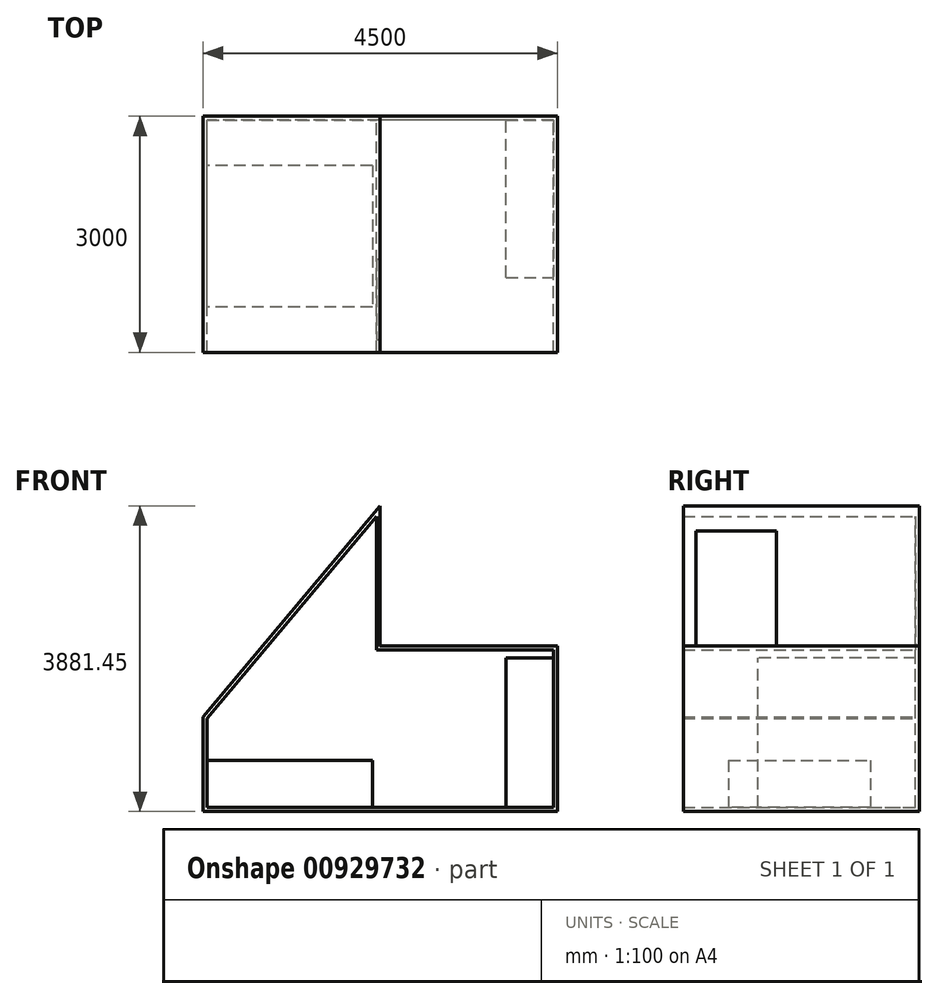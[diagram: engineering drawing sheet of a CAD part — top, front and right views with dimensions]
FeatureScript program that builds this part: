
annotation { "Feature Type Name" : "Feature", "Feature Type Description" : "" }
export const myFeature = defineFeature(function(context is Context, id is Id, definition is map)
    precondition{}
    {
        {
            var Q0;
            Q0=qCreatedBy(makeId("Front.planeOp"),FACE);
            var sketch = newSketch(context, id + "F0", { "sketchPlane" : qUnion([Q0])});
            skLineSegment(sketch, "E0.bottom", {"start": v(98.96, 0) * mm, "end": v(-4401.04, 0) * mm});
            skLineSegment(sketch, "E0.top", {"start": v(98.96, 2100) * mm, "end": v(-2151.04, 2100) * mm});
            skLineSegment(sketch, "E0.left", {"start": v(98.96, 0) * mm, "end": v(98.96, 2100) * mm});
            skLineSegment(sketch, "E0.right", {"start": v(-4401.04, 0) * mm, "end": v(-4401.04, 1200) * mm});
            skLineSegment(sketch, "E1", {"start": v(-4401.04, 1200) * mm, "end": v(-2151.04, 3881.45) * mm});
            skPoint(sketch, "E1.endSnap0", {"position": v(-2151.04, 2100) * mm});
            skLineSegment(sketch, "E2", {"start": v(-2151.04, 3881.45) * mm, "end": v(-2151.04, 2100) * mm});
            skPoint(sketch, "E3.orphan", {"position": v(-4401.04, 2100) * mm});
            skSolve(sketch);
        }
        {
            var Q0;
            Q0 = qSketchRegion(id + "F0", true);
            extrude(context, id + "F1", {"entities" : qUnion([Q0]), "depth" : 3000 * mm, "offsetDistance" : 25 * mm});
        }
        {
            var Q0;
            Q0=makeQuery(id+"F1.opExtrude","CAP_FACE",FACE,{"disambiguationData":[OSD([sQuery(id+"F0.wireOp",EDGE,"E0.bottom"),sQuery(id+"F0.wireOp",EDGE,"E0.top"),sQuery(id+"F0.wireOp",EDGE,"E0.left"),sQuery(id+"F0.wireOp",EDGE,"E0.right"),sQuery(id+"F0.wireOp",EDGE,"E1"),sQuery(id+"F0.wireOp",EDGE,"E2")])],"isStart":false});
            shell(context, id + "F2", {"entities" : qUnion([Q0]), "thickness" : 50 * mm});
        }
        {
            var Q0;
            Q0=makeQuery(id+"F1.opExtrude","SWEPT_FACE",FACE,{"disambiguationData":[OSD([sQuery(id+"F0.wireOp",EDGE,"E2")])]});
            var sketch = newSketch(context, id + "F3", { "sketchPlane" : qUnion([Q0])});
            skPoint(sketch, "E4.middle", {"position": v(-1500, 2100) * mm});
            skPoint(sketch, "E4.top.start.orphan", {"position": v(-2296.31, 1072.77) * mm});
            skPoint(sketch, "E5.orphan", {"position": v(-703.69, 1072.77) * mm});
            skLineSegment(sketch, "E6.bottom", {"start": v(-2837.74, 2100) * mm, "end": v(-1817.95, 2100) * mm});
            skLineSegment(sketch, "E6.top", {"start": v(-2837.74, 3564.25) * mm, "end": v(-1817.95, 3564.25) * mm});
            skLineSegment(sketch, "E6.left", {"start": v(-2837.74, 2100) * mm, "end": v(-2837.74, 3564.25) * mm});
            skLineSegment(sketch, "E6.right", {"start": v(-1817.95, 2100) * mm, "end": v(-1817.95, 3564.25) * mm});
            skPoint(sketch, "E4.left.start.orphan", {"position": v(-2296.31, 3127.23) * mm});
            skPoint(sketch, "E7.orphan", {"position": v(-2296.31, 2100) * mm});
            skPoint(sketch, "E4.right.end.orphan", {"position": v(-703.69, 2100) * mm});
            skPoint(sketch, "E4.right.start.orphan", {"position": v(-703.69, 3127.23) * mm});
            skSolve(sketch);
        }
        {
            var Q0;
            Q0 = qSketchRegion(id + "F3", true);
            extrude(context, id + "F4", {"entities" : qUnion([Q0]), "operationType" : NewBodyOperationType.REMOVE, "endBound" : BoundingType.UP_TO_NEXT, "oppositeDirection" : true, "depth" : 25 * mm, "offsetDistance" : 25 * mm});
        }
        {
            var Q0;
            Q0=makeQuery(id+"F2.opShell","OFFSET_FACE",FACE,{"disambiguationData":[OSD([sQuery(id+"F0.wireOp",EDGE,"E0.bottom")])]});
            var sketch = newSketch(context, id + "F5", { "sketchPlane" : qUnion([Q0])});
            skLineSegment(sketch, "E8.bottom", {"start": v(-2251.04, -625) * mm, "end": v(-4351.04, -625) * mm});
            skLineSegment(sketch, "E8.top", {"start": v(-2251.04, -2425) * mm, "end": v(-4351.04, -2425) * mm});
            skLineSegment(sketch, "E8.left", {"start": v(-2251.04, -625) * mm, "end": v(-2251.04, -2425) * mm});
            skPoint(sketch, "E8.middle", {"position": v(-4351.04, -1525) * mm});
            skLineSegment(sketch, "E9", {"start": v(-4351.04, -2425) * mm, "end": v(-4351.04, -625) * mm});
            skPoint(sketch, "E8.right.end.orphan", {"position": v(-6451.04, -2425) * mm});
            skPoint(sketch, "E10.orphan", {"position": v(-6451.04, -625) * mm});
            skSolve(sketch);
        }
        {
            var Q0;
            Q0 = qSketchRegion(id + "F5", true);
            extrude(context, id + "F6", {"entities" : qUnion([Q0]), "operationType" : NewBodyOperationType.ADD, "depth" : 600 * mm, "offsetDistance" : 25 * mm});
        }
        {
            var Q0;
            Q0=makeQuery(id+"F2.opShell","OFFSET_FACE",FACE,{"disambiguationData":[OSD([sQuery(id+"F0.wireOp",EDGE,"E0.left")])]});
            var sketch = newSketch(context, id + "F7", { "sketchPlane" : qUnion([Q0])});
            skLineSegment(sketch, "E11.bottom", {"start": v(50, 50) * mm, "end": v(2050, 50) * mm});
            skLineSegment(sketch, "E11.top", {"start": v(50, 1950) * mm, "end": v(2050, 1950) * mm});
            skLineSegment(sketch, "E11.left", {"start": v(50, 50) * mm, "end": v(50, 1950) * mm});
            skLineSegment(sketch, "E11.right", {"start": v(2050, 50) * mm, "end": v(2050, 1950) * mm});
            skSolve(sketch);
        }
        {
            var Q0;
            Q0 = qSketchRegion(id + "F7", true);
            extrude(context, id + "F8", {"entities" : qUnion([Q0]), "operationType" : NewBodyOperationType.ADD, "depth" : 600 * mm, "offsetDistance" : 25 * mm});
        }
    });
